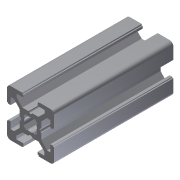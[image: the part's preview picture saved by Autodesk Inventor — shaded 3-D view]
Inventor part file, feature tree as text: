
AUTODESK INVENTOR PART (.ipt)
format: ipt  version: 2011 (Build 150239000, 239)  size: 180,736 bytes
history: native  units: in
note: dims shown in document units (in); Inventor stores cm internally (conversion verified against a paired STEP export)
features: plane x3, extrude x1, sketch x1
ambient origin geometry x8: Origin, YZ Plane, XZ Plane, XY Plane, X Axis, Y Axis, Z Axis, Center Point
bodies: Solid1 (feature_tree)
feature tree (5):
  extrude  "Extrusion1"  [1 undecoded]
  plane  "Work Plane1"
  plane  "Work Plane2"
  plane  "Work Plane3"
  sketch  "Sketch1"  dims[d0=2.0in d1=0.0in d2=-0.5in]
note: 1 required parameter value undecoded (feature->parameter linkage not recoverable at this tier; creation-order binding heuristic only, values carry confidence <= 0.55)
